# Revit family: Gira_238300
name_source: partatom
category: Electrical Fixtures
revit_build: Autodesk Revit 2017 (Build: 20160225_1515(x64)
units: mm (PartAtom-declared; Revit-internal decimal feet)

## family parameters
Cut with Voids When Loaded = No
Host = Face
Maintain Annotation Orientation = No
Part Type = Normal
Room Calculation Point = No
Round Connector Dimension = Use Diameter
Shared = No

## types (1)
- S3000 uni.LED pow.booster DRA Electronics
    App control via Bluetooth = No
    Applicable with button = No
    Applicable with infrared button = No
    Applicable with movement sensor = No
    Applicable with presence indicator = No
    Applicable with time switch/timer = No
    Applicable with transmission button = No
    BIM = https://media.live.bim.site X1 REG KNX.rfa
    BIMSITE_PRODUCT_ID = 44f2ea9102cb048f289e55444001b083e8bfdadf
    Bus connection included = No
    Cost = 0 $
    Default Elevation = 1219 mm
    Description = S3000 uni.LED pow.booster DRA Elec. System 3000 universal LED power booster DRA,DRA Features: - Switching and dimming light bulbs, HV halogen lamps, electronic transformers for halogen, inductive transformers for halogen, HV LED or compact fluorescent lamps. - Operation is via upstream dimmer. - The connected loads are supplied via a common load line. - Electronic excess-temperature protection.,Notes : - If the ambient temperature is higher than 45 C, the connected load must be reduced. - Maximum load and number of power boosters depend on dimmer. Refer to the technical appendix or operating instructions for a reference list.
    Dimming phase cut-off = No
    Dimming phase cut-on = No
    GTIN = 4010337031383
    HAN = 238300
    Halogen free = No
    HeinzeBIM = https://www.heinze.de
    Light value memory = No
    Manufacturer = Gira
    Material = Sonstige (*de-DE)
    Material quality = Sonstige (*de-DE)
    Number of inputs = 0
    Radio frequent bidirectional = No
    Serial dimmer = No
    Surface finishing = Not applicable
    Surface protection = Sonstige (*de-DE)
    Transparent = No
    Type of load = Universal and LED Retrofit
    URL = https://www.gira.de
    With label area = No

## geometry (parser evidence)
native form markers: Blend x2, Sweep x3
no freeform markers — native parametric forms only
